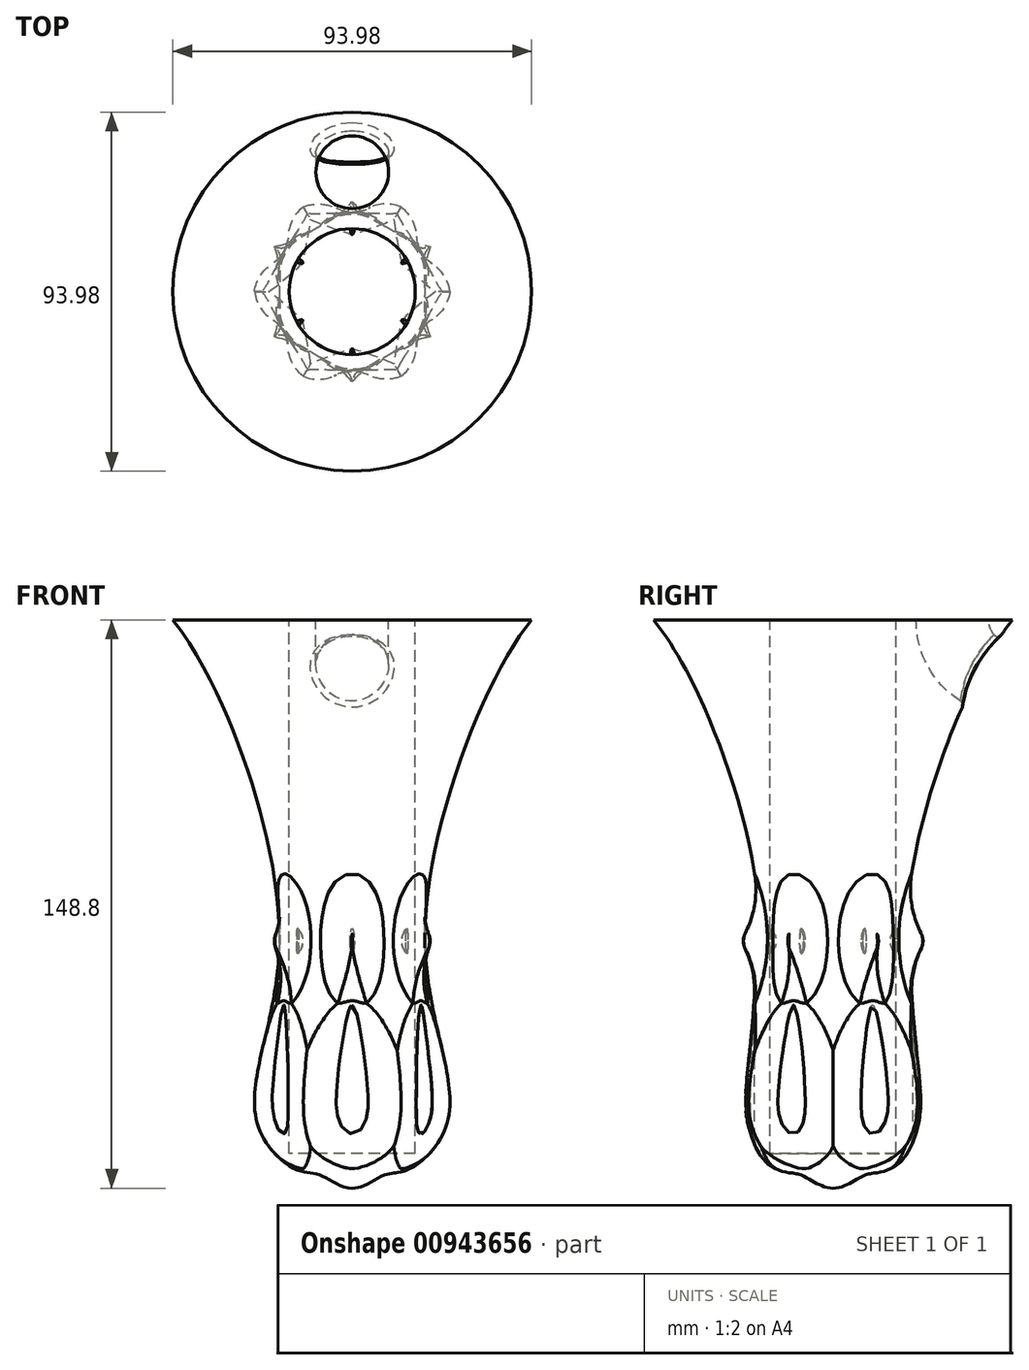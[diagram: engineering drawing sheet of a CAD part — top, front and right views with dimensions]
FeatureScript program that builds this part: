
annotation { "Feature Type Name" : "Feature", "Feature Type Description" : "" }
export const myFeature = defineFeature(function(context is Context, id is Id, definition is map)
    precondition{}
    {
        {
            var Q0;
            Q0=qCreatedBy(makeId("Front.planeOp"),FACE);
            var sketch = newSketch(context, id + "F0", { "sketchPlane" : qUnion([Q0])});
            skLineSegment(sketch, "E0", {"start": v(0, 0) * mm, "end": v(-16.51, 0) * mm});
            skLineSegment(sketch, "E1", {"start": v(-16.51, 0) * mm, "end": v(-16.51, 139.7) * mm});
            skLineSegment(sketch, "E2", {"start": v(-16.51, 139.7) * mm, "end": v(-47, 139.7) * mm});
            skPoint(sketch, "E3.4.internal.snap0", {"position": v(-8.26, 0) * mm});
            skFitSpline(sketch, "E3", {"points": [v(-47, 139.7) * mm, v(-19.1, 56.32) * mm, v(-25.28, 9.08) * mm, v(-14.37, -4.32) * mm, v(-8.26, -5.7) * mm, v(0, -9.1) * mm], "startDerivative": vector(103.36, -126) * mm, "endDerivative": vector(83.09, 0) * mm});
            skLineSegment(sketch, "E4", {"start": v(0, 0) * mm, "end": v(0, -9.1) * mm});
            skSolve(sketch);
        }
        {
            var Q0;
            Q0=qSketchRegion(id+"F0",true);
            var Q1;
            Q1=sQuery(id+"F0.wireOp",EDGE,"E4");
            revolve(context, id + "F1", {"surfaceOperationType" : NewSurfaceOperationType.NEW, "entities" : qUnion([Q0]), "axis" : qUnion([Q1]), "revolveType" : RevolveType.FULL});
        }
        {
            var Q0;
            Q0=qCreatedBy(makeId("Top.planeOp"),FACE);
            var sketch = newSketch(context, id + "F2", { "sketchPlane" : qUnion([Q0])});
            skCircle(sketch, "E5", {"center": v(0, -29.76) * mm, "radius": 9 * mm});
            skCircle(sketch, "E6.1.0", {"center": v(25.77, -14.88) * mm, "radius": 9 * mm});
            skCircle(sketch, "E6.2.0", {"center": v(25.77, 14.88) * mm, "radius": 9 * mm});
            skCircle(sketch, "E6.3.0", {"center": v(0, 29.76) * mm, "radius": 9 * mm});
            skCircle(sketch, "E6.4.0", {"center": v(-25.77, 14.88) * mm, "radius": 9 * mm});
            skCircle(sketch, "E6.5.0", {"center": v(-25.77, -14.88) * mm, "radius": 9 * mm});
            skPoint(sketch, "E6.center", {"position": v(0, 0) * mm});
            skSolve(sketch);
        }
        {
            var Q0;
            Q0=makeQuery(id+"F2.imprint","IMPRINT",FACE,{"disambiguationData":[TD([[makeQuery(id+"F2.imprint","IMPRINT",EDGE,{"derivedFrom":sQuery(id+"F2.wireOp",EDGE,"E5")}),1.0]])]});
            var Q1;
            Q1=makeQuery(id+"F2.imprint","IMPRINT",FACE,{"disambiguationData":[TD([[makeQuery(id+"F2.imprint","IMPRINT",EDGE,{"derivedFrom":sQuery(id+"F2.wireOp",EDGE,"E6.1.0")}),1.0]])]});
            var Q2;
            Q2=makeQuery(id+"F2.imprint","IMPRINT",FACE,{"disambiguationData":[TD([[makeQuery(id+"F2.imprint","IMPRINT",EDGE,{"derivedFrom":sQuery(id+"F2.wireOp",EDGE,"E6.5.0")}),1.0]])]});
            var Q3;
            Q3=makeQuery(id+"F2.imprint","IMPRINT",FACE,{"disambiguationData":[TD([[makeQuery(id+"F2.imprint","IMPRINT",EDGE,{"derivedFrom":sQuery(id+"F2.wireOp",EDGE,"E6.4.0")}),1.0]])]});
            var Q4;
            Q4=makeQuery(id+"F2.imprint","IMPRINT",FACE,{"disambiguationData":[TD([[makeQuery(id+"F2.imprint","IMPRINT",EDGE,{"derivedFrom":sQuery(id+"F2.wireOp",EDGE,"E6.2.0")}),1.0]])]});
            var Q5;
            Q5=makeQuery(id+"F2.imprint","IMPRINT",FACE,{"disambiguationData":[TD([[makeQuery(id+"F2.imprint","IMPRINT",EDGE,{"derivedFrom":sQuery(id+"F2.wireOp",EDGE,"E6.3.0")}),1.0]])]});
            extrude(context, id + "F3", {"entities" : qUnion([Q0, Q1, Q2, Q3, Q4, Q5]), "operationType" : NewBodyOperationType.REMOVE, "depth" : 54.1 * mm, "offsetDistance" : 25.4 * mm});
        }
        {
            var Q0;
            Q0=makeQuery(id+"F3.boolean.opBoolean","COPY",FACE,{"derivedFrom":makeQuery(id+"F3.opExtrude","SWEPT_FACE",FACE,{"disambiguationData":[OSD([sQuery(id+"F2.wireOp",EDGE,"E5")])]})});
            var Q1;
            Q1=makeQuery(id+"F3.boolean.opBoolean","COPY",FACE,{"derivedFrom":makeQuery(id+"F3.opExtrude","SWEPT_FACE",FACE,{"disambiguationData":[OSD([sQuery(id+"F2.wireOp",EDGE,"E6.1.0")])]})});
            var Q2;
            Q2=makeQuery(id+"F3.boolean.opBoolean","COPY",FACE,{"derivedFrom":makeQuery(id+"F3.opExtrude","SWEPT_FACE",FACE,{"disambiguationData":[OSD([sQuery(id+"F2.wireOp",EDGE,"E6.2.0")])]})});
            var Q3;
            Q3=makeQuery(id+"F3.boolean.opBoolean","INTERSECT",EDGE,{"derivedFrom":[makeQuery(id+"F1.opRevolve","SWEPT_FACE",FACE,{"disambiguationData":[OSD([sQuery(id+"F0.wireOp",EDGE,"E3")])]}),makeQuery(id+"F3.opExtrude","SWEPT_FACE",FACE,{"disambiguationData":[OSD([sQuery(id+"F2.wireOp",EDGE,"E6.3.0")])]})]});
            var Q4;
            Q4=makeQuery(id+"F3.boolean.opBoolean","COPY",FACE,{"derivedFrom":makeQuery(id+"F3.opExtrude","SWEPT_FACE",FACE,{"disambiguationData":[OSD([sQuery(id+"F2.wireOp",EDGE,"E6.4.0")])]})});
            var Q5;
            Q5=makeQuery(id+"F3.boolean.opBoolean","COPY",FACE,{"derivedFrom":makeQuery(id+"F3.opExtrude","SWEPT_FACE",FACE,{"disambiguationData":[OSD([sQuery(id+"F2.wireOp",EDGE,"E6.5.0")])]})});
            fillet(context, id + "F4", {"entities" : qUnion([Q0, Q1, Q2, Q3, Q4, Q5]), "radius" : 10.16 * mm, "tangentPropagation" : true, "allowEdgeOverflow" : false});
        }
        {
            var Q0;
            Q0=qCreatedBy(makeId("Top.planeOp"),FACE);
            cPlane(context, id + "F5", {"entities" : qUnion([Q0]), "cplaneType" : CPlaneType.OFFSET, "offset" : 55.63 * mm, "width" : 152.4 * mm, "height" : 152.4 * mm});
        }
        {
            var Q0;
            Q0=qCreatedBy(id+"F5.planeOp",FACE);
            var sketch = newSketch(context, id + "F6", { "sketchPlane" : qUnion([Q0])});
            skEllipse(sketch, "E7", {"center": v(0, -19.24) * mm, "majorRadius": 4.3 * mm, "minorRadius": 0.73 * mm, "majorAxis": v(0, -1)});
            skEllipse(sketch, "E8.1.0", {"center": v(16.67, -9.62) * mm, "majorRadius": 4.3 * mm, "minorRadius": 0.73 * mm, "majorAxis": v(0.87, -0.5)});
            skEllipse(sketch, "E8.2.0", {"center": v(16.67, 9.62) * mm, "majorRadius": 4.3 * mm, "minorRadius": 0.73 * mm, "majorAxis": v(0.87, 0.5)});
            skEllipse(sketch, "E8.3.0", {"center": v(0, 19.24) * mm, "majorRadius": 4.3 * mm, "minorRadius": 0.73 * mm, "majorAxis": v(0, 1)});
            skEllipse(sketch, "E8.4.0", {"center": v(-16.67, 9.62) * mm, "majorRadius": 4.3 * mm, "minorRadius": 0.73 * mm, "majorAxis": v(-0.87, 0.5)});
            skEllipse(sketch, "E8.5.0", {"center": v(-16.67, -9.62) * mm, "majorRadius": 4.3 * mm, "minorRadius": 0.73 * mm, "majorAxis": v(-0.87, -0.5)});
            skPoint(sketch, "E8.center", {"position": v(0, 0) * mm});
            skLineSegment(sketch, "E9", {"start": v(-16.67, -9.62) * mm, "end": v(-16.3, -10.25) * mm});
            skLineSegment(sketch, "E10", {"start": v(-16.67, -9.62) * mm, "end": v(-17.03, -9) * mm});
            skLineSegment(sketch, "E11", {"start": v(0, -19.24) * mm, "end": v(-0.73, -19.24) * mm});
            skLineSegment(sketch, "E12", {"start": v(0, -19.24) * mm, "end": v(0.73, -19.24) * mm});
            skLineSegment(sketch, "E13", {"start": v(16.67, -9.62) * mm, "end": v(16.3, -10.25) * mm});
            skLineSegment(sketch, "E14", {"start": v(16.67, -9.62) * mm, "end": v(17.03, -9) * mm});
            skLineSegment(sketch, "E15", {"start": v(16.67, 9.62) * mm, "end": v(17.03, 9) * mm});
            skLineSegment(sketch, "E16", {"start": v(16.67, 9.62) * mm, "end": v(16.3, 10.25) * mm});
            skLineSegment(sketch, "E17", {"start": v(0, 19.24) * mm, "end": v(-0.73, 19.24) * mm});
            skLineSegment(sketch, "E18", {"start": v(0, 19.24) * mm, "end": v(0.73, 19.24) * mm});
            skLineSegment(sketch, "E19", {"start": v(-16.67, 9.62) * mm, "end": v(-17.03, 9) * mm});
            skLineSegment(sketch, "E20", {"start": v(-16.67, 9.62) * mm, "end": v(-16.3, 10.25) * mm});
            skSolve(sketch);
        }
        {
            var Q0;
            {var subQ0=sQuery(id+"F6.wireOp",EDGE,"E9");Q0=makeQuery(id+"F6.imprint","IMPRINT",FACE,{"disambiguationData":[TD([[makeQuery(id+"F6.imprint","IMPRINT",EDGE,{"derivedFrom":subQ0}),-1.0]])]});}
            var Q1;
            Q1=sQuery(id+"F6.wireOp",EDGE,"E9");
            revolve(context, id + "F7", {"operationType" : NewBodyOperationType.ADD, "surfaceOperationType" : NewSurfaceOperationType.NEW, "entities" : qUnion([Q0]), "axis" : qUnion([Q1]), "revolveType" : RevolveType.FULL});
        }
        {
            var Q0;
            {var subQ0=sQuery(id+"F6.wireOp",EDGE,"E11");Q0=makeQuery(id+"F6.imprint","IMPRINT",FACE,{"disambiguationData":[TD([[makeQuery(id+"F6.imprint","IMPRINT",EDGE,{"derivedFrom":subQ0}),1.0]])]});}
            var Q1;
            Q1=sQuery(id+"F6.wireOp",EDGE,"E12");
            revolve(context, id + "F8", {"operationType" : NewBodyOperationType.ADD, "surfaceOperationType" : NewSurfaceOperationType.NEW, "entities" : qUnion([Q0]), "axis" : qUnion([Q1]), "revolveType" : RevolveType.FULL});
        }
        {
            var Q0;
            {var subQ0=sQuery(id+"F6.wireOp",EDGE,"E13");Q0=makeQuery(id+"F6.imprint","IMPRINT",FACE,{"disambiguationData":[TD([[makeQuery(id+"F6.imprint","IMPRINT",EDGE,{"derivedFrom":subQ0}),-1.0]])]});}
            var Q1;
            Q1=sQuery(id+"F6.wireOp",EDGE,"E13");
            revolve(context, id + "F9", {"operationType" : NewBodyOperationType.ADD, "surfaceOperationType" : NewSurfaceOperationType.NEW, "entities" : qUnion([Q0]), "axis" : qUnion([Q1]), "revolveType" : RevolveType.FULL});
        }
        {
            var Q0;
            {var subQ0=sQuery(id+"F6.wireOp",EDGE,"E15");Q0=makeQuery(id+"F6.imprint","IMPRINT",FACE,{"disambiguationData":[TD([[makeQuery(id+"F6.imprint","IMPRINT",EDGE,{"derivedFrom":subQ0}),-1.0]])]});}
            var Q1;
            Q1=sQuery(id+"F6.wireOp",EDGE,"E16");
            revolve(context, id + "F10", {"operationType" : NewBodyOperationType.ADD, "surfaceOperationType" : NewSurfaceOperationType.NEW, "entities" : qUnion([Q0]), "axis" : qUnion([Q1]), "revolveType" : RevolveType.FULL});
        }
        {
            var Q0;
            {var subQ0=sQuery(id+"F6.wireOp",EDGE,"E17");Q0=makeQuery(id+"F6.imprint","IMPRINT",FACE,{"disambiguationData":[TD([[makeQuery(id+"F6.imprint","IMPRINT",EDGE,{"derivedFrom":subQ0}),1.0]])]});}
            var Q1;
            Q1=sQuery(id+"F6.wireOp",EDGE,"E17");
            revolve(context, id + "F11", {"operationType" : NewBodyOperationType.ADD, "surfaceOperationType" : NewSurfaceOperationType.NEW, "entities" : qUnion([Q0]), "axis" : qUnion([Q1]), "revolveType" : RevolveType.FULL});
        }
        {
            var Q0;
            {var subQ0=sQuery(id+"F6.wireOp",EDGE,"E19");Q0=makeQuery(id+"F6.imprint","IMPRINT",FACE,{"disambiguationData":[TD([[makeQuery(id+"F6.imprint","IMPRINT",EDGE,{"derivedFrom":subQ0}),1.0]])]});}
            var Q1;
            Q1=sQuery(id+"F6.wireOp",EDGE,"E20");
            revolve(context, id + "F12", {"operationType" : NewBodyOperationType.ADD, "surfaceOperationType" : NewSurfaceOperationType.NEW, "entities" : qUnion([Q0]), "axis" : qUnion([Q1]), "revolveType" : RevolveType.FULL});
        }
        {
            var Q0;
            Q0=makeQuery(id+"F7.boolean.opBoolean","INTERSECT",EDGE,{"derivedFrom":[makeQuery(id+"F4.opFillet","SPLIT",FACE,{"disambiguationData":[OD(1.0)],"derivedFrom":makeQuery(id+"F1.opRevolve","SWEPT_FACE",FACE,{"disambiguationData":[OSD([sQuery(id+"F0.wireOp",EDGE,"E3")])]})}),makeQuery(id+"F7.opRevolve","SWEPT_FACE",FACE,{"disambiguationData":[OSD([sQuery(id+"F6.wireOp",EDGE,"E8.5.0")])]})]});
            var Q1;
            Q1=makeQuery(id+"F8.boolean.opBoolean","INTERSECT",EDGE,{"derivedFrom":[makeQuery(id+"F4.opFillet","SPLIT",FACE,{"disambiguationData":[OD(1.0)],"derivedFrom":makeQuery(id+"F1.opRevolve","SWEPT_FACE",FACE,{"disambiguationData":[OSD([sQuery(id+"F0.wireOp",EDGE,"E3")])]})}),makeQuery(id+"F8.opRevolve","SWEPT_FACE",FACE,{"disambiguationData":[OSD([sQuery(id+"F6.wireOp",EDGE,"E7")])]})]});
            var Q2;
            Q2=makeQuery(id+"F9.boolean.opBoolean","INTERSECT",EDGE,{"derivedFrom":[makeQuery(id+"F4.opFillet","SPLIT",FACE,{"disambiguationData":[OD(1.0)],"derivedFrom":makeQuery(id+"F1.opRevolve","SWEPT_FACE",FACE,{"disambiguationData":[OSD([sQuery(id+"F0.wireOp",EDGE,"E3")])]})}),makeQuery(id+"F9.opRevolve","SWEPT_FACE",FACE,{"disambiguationData":[OSD([sQuery(id+"F6.wireOp",EDGE,"E8.1.0")])]})]});
            var Q3;
            Q3=makeQuery(id+"F10.boolean.opBoolean","INTERSECT",EDGE,{"derivedFrom":[makeQuery(id+"F4.opFillet","SPLIT",FACE,{"disambiguationData":[OD(1.0)],"derivedFrom":makeQuery(id+"F1.opRevolve","SWEPT_FACE",FACE,{"disambiguationData":[OSD([sQuery(id+"F0.wireOp",EDGE,"E3")])]})}),makeQuery(id+"F10.opRevolve","SWEPT_FACE",FACE,{"disambiguationData":[OSD([sQuery(id+"F6.wireOp",EDGE,"E8.2.0")])]})]});
            var Q4;
            Q4=makeQuery(id+"F11.boolean.opBoolean","INTERSECT",EDGE,{"derivedFrom":[makeQuery(id+"F4.opFillet","SPLIT",FACE,{"disambiguationData":[OD(1.0)],"derivedFrom":makeQuery(id+"F1.opRevolve","SWEPT_FACE",FACE,{"disambiguationData":[OSD([sQuery(id+"F0.wireOp",EDGE,"E3")])]})}),makeQuery(id+"F11.opRevolve","SWEPT_FACE",FACE,{"disambiguationData":[OSD([sQuery(id+"F6.wireOp",EDGE,"E8.3.0")])]})]});
            var Q5;
            Q5=makeQuery(id+"F12.boolean.opBoolean","INTERSECT",EDGE,{"derivedFrom":[makeQuery(id+"F4.opFillet","SPLIT",FACE,{"disambiguationData":[OD(1.0)],"derivedFrom":makeQuery(id+"F1.opRevolve","SWEPT_FACE",FACE,{"disambiguationData":[OSD([sQuery(id+"F0.wireOp",EDGE,"E3")])]})}),makeQuery(id+"F12.opRevolve","SWEPT_FACE",FACE,{"disambiguationData":[OSD([sQuery(id+"F6.wireOp",EDGE,"E8.4.0")])]})]});
            fillet(context, id + "F13", {"entities" : qUnion([Q0, Q1, Q2, Q3, Q4, Q5]), "radius" : 25.4 * mm, "tangentPropagation" : true, "allowEdgeOverflow" : false});
        }
        {
            var Q0;
            Q0=makeQuery(id+"F1.opRevolve","SWEPT_FACE",FACE,{"disambiguationData":[OSD([sQuery(id+"F0.wireOp",EDGE,"E2")])]});
            var sketch = newSketch(context, id + "F14", { "sketchPlane" : qUnion([Q0])});
            skLineSegment(sketch, "E21", {"start": v(0, 47) * mm, "end": v(0, 0) * mm});
            skLineSegment(sketch, "E22", {"start": v(0, -0.48) * mm, "end": v(0, 31.27) * mm});
            skCircle(sketch, "E23", {"center": v(0, 31.27) * mm, "radius": 9.53 * mm});
            skLineSegment(sketch, "E24", {"start": v(0, 47) * mm, "end": v(-12.82, 47) * mm});
            skSolve(sketch);
        }
        {
            var Q0;
            {var subQ0=sQuery(id+"F14.wireOp",EDGE,"E22");var subQ1=sQuery(id+"F14.wireOp",EDGE,"E21");var subQ2=makeQuery(id+"F14.imprint","INTERSECT",VERTEX,{"derivedFrom":[subQ1,subQ0]});Q0=makeQuery(id+"F14.imprint","IMPRINT",FACE,{"disambiguationData":[TD([[makeQuery(id+"F14.imprint","IMPRINT",EDGE,{"disambiguationData":[TD([[subQ2,1.0]])],"derivedFrom":subQ1}),-1.0]])]});}
            var Q1;
            {var subQ0=sQuery(id+"F14.wireOp",EDGE,"E22");var subQ1=sQuery(id+"F14.wireOp",EDGE,"E21");var subQ2=makeQuery(id+"F14.imprint","INTERSECT",VERTEX,{"derivedFrom":[subQ1,subQ0]});Q1=makeQuery(id+"F14.imprint","IMPRINT",FACE,{"disambiguationData":[TD([[makeQuery(id+"F14.imprint","IMPRINT",EDGE,{"disambiguationData":[TD([[subQ2,1.0]])],"derivedFrom":subQ1}),1.0]])]});}
            var Q2;
            Q2=sQuery(id+"F14.wireOp",EDGE,"E24");
            revolve(context, id + "F15", {"operationType" : NewBodyOperationType.REMOVE, "surfaceOperationType" : NewSurfaceOperationType.NEW, "entities" : qUnion([Q0, Q1]), "axis" : qUnion([Q2]), "revolveType" : RevolveType.FULL, "oppositeDirection" : true});
        }
        {
            var Q0;
            Q0=makeQuery(id+"F15.boolean.opBoolean","INTERSECT",EDGE,{"derivedFrom":[makeQuery(id+"F4.opFillet","SPLIT",FACE,{"disambiguationData":[OD(1.0)],"derivedFrom":makeQuery(id+"F1.opRevolve","SWEPT_FACE",FACE,{"disambiguationData":[OSD([sQuery(id+"F0.wireOp",EDGE,"E3")])]})}),makeQuery(id+"F15.opRevolve","SWEPT_FACE",FACE,{"disambiguationData":[OSD([sQuery(id+"F14.wireOp",EDGE,"E23")])]})]});
            fillet(context, id + "F16", {"entities" : qUnion([Q0]), "radius" : 1.27 * mm, "tangentPropagation" : true, "allowEdgeOverflow" : false});
        }
    });
